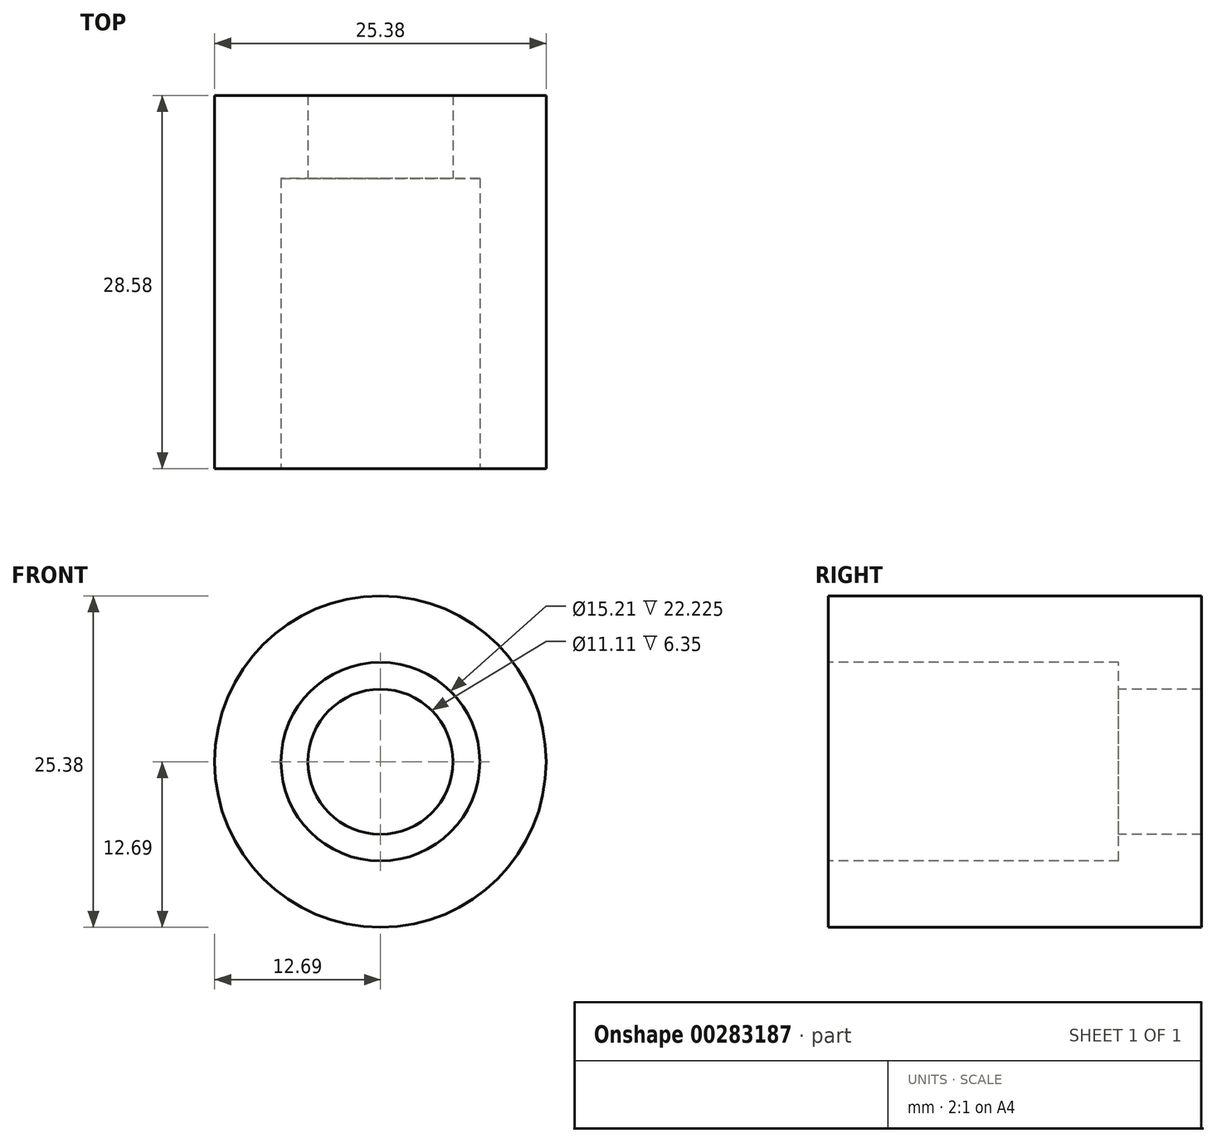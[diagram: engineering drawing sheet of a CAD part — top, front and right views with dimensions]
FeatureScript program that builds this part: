
annotation { "Feature Type Name" : "Feature", "Feature Type Description" : "" }
export const myFeature = defineFeature(function(context is Context, id is Id, definition is map)
    precondition{}
    {
        {
            var Q0;
            Q0=qCreatedBy(makeId("Front.planeOp"),FACE);
            var sketch = newSketch(context, id + "F0", { "sketchPlane" : qUnion([Q0])});
            skCircle(sketch, "E0", {"center": v(0, 0) * mm, "radius": 5.56 * mm});
            skCircle(sketch, "E1", {"center": v(0, 0) * mm, "radius": 7.6 * mm});
            skCircle(sketch, "E2", {"center": v(0, 0) * mm, "radius": 12.69 * mm});
            skSolve(sketch);
        }
        {
            var Q0;
            Q0 = qSketchRegion(id + "F0", true);
            var Q1;
            Q1=makeQuery(id+"F0.imprint","IMPRINT",FACE,{"disambiguationData":[TD([[makeQuery(id+"F0.imprint","IMPRINT",EDGE,{"derivedFrom":sQuery(id+"F0.wireOp",EDGE,"E0")}),1.0]])]});
            var Q2;
            Q2=makeQuery(id+"F0.imprint","IMPRINT",FACE,{"disambiguationData":[TD([[makeQuery(id+"F0.imprint","IMPRINT",EDGE,{"derivedFrom":sQuery(id+"F0.wireOp",EDGE,"E0")}),-1.0]])]});
            extrude(context, id + "F1", {"entities" : qUnion([Q0, Q1, Q2]), "depth" : 28.57 * mm});
        }
        {
            var Q0;
            Q0=makeQuery(id+"F1.opExtrude","CAP_FACE",FACE,{"disambiguationData":[OSD([sQuery(id+"F0.wireOp",EDGE,"E2")])],"isStart":false});
            var sketch = newSketch(context, id + "F2", { "sketchPlane" : qUnion([Q0])});
            skCircle(sketch, "E3", {"center": v(0, 0) * mm, "radius": 7.6 * mm});
            skSolve(sketch);
        }
        {
            var Q0;
            Q0=makeQuery(id+"F2.imprint","IMPRINT",FACE,{"disambiguationData":[TD([[makeQuery(id+"F2.imprint","IMPRINT",EDGE,{"derivedFrom":sQuery(id+"F2.wireOp",EDGE,"E3")}),1.0]])]});
            extrude(context, id + "F3", {"entities" : qUnion([Q0]), "operationType" : NewBodyOperationType.REMOVE, "oppositeDirection" : true, "depth" : 22.22 * mm});
        }
        {
            var Q0;
            Q0=makeQuery(id+"F3.boolean.opBoolean","COPY",FACE,{"derivedFrom":makeQuery(id+"F3.opExtrude","CAP_FACE",FACE,{"disambiguationData":[OSD([sQuery(id+"F2.wireOp",EDGE,"E3")])],"isStart":false})});
            var sketch = newSketch(context, id + "F4", { "sketchPlane" : qUnion([Q0])});
            skCircle(sketch, "E4", {"center": v(0, 0) * mm, "radius": 5.56 * mm});
            skSolve(sketch);
        }
        {
            var Q0;
            Q0=makeQuery(id+"F4.imprint","IMPRINT",FACE,{"disambiguationData":[TD([[makeQuery(id+"F4.imprint","IMPRINT",EDGE,{"derivedFrom":sQuery(id+"F4.wireOp",EDGE,"E4")}),1.0]])]});
            extrude(context, id + "F5", {"entities" : qUnion([Q0]), "operationType" : NewBodyOperationType.REMOVE, "endBound" : BoundingType.THROUGH_ALL, "oppositeDirection" : true, "depth" : 25.4 * mm});
        }
    });
